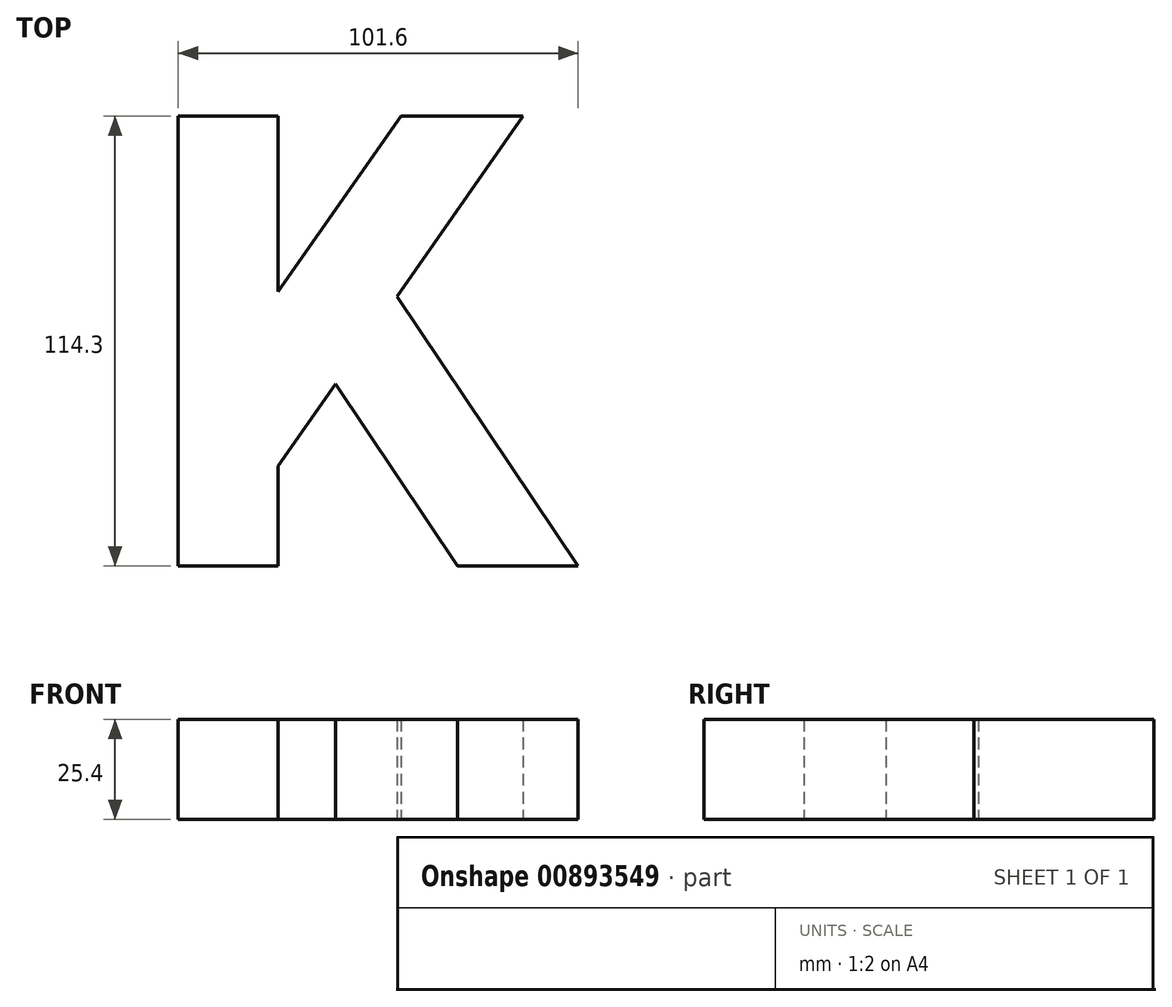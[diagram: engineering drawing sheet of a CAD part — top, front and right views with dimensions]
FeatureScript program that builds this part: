
annotation { "Feature Type Name" : "Feature", "Feature Type Description" : "" }
export const myFeature = defineFeature(function(context is Context, id is Id, definition is map)
    precondition{}
    {
        {
            var Q0;
            Q0=qCreatedBy(makeId("Top.planeOp"),FACE);
            var sketch = newSketch(context, id + "F0", { "sketchPlane" : qUnion([Q0])});
            skLineSegment(sketch, "E0", {"start": v(-39.97, 68.1) * mm, "end": v(-39.97, -46.2) * mm});
            skLineSegment(sketch, "E1", {"start": v(-39.97, -46.2) * mm, "end": v(-14.57, -46.2) * mm});
            skLineSegment(sketch, "E2", {"start": v(-14.57, -46.2) * mm, "end": v(-14.57, -20.8) * mm});
            skLineSegment(sketch, "E3", {"start": v(-14.57, -20.8) * mm, "end": v(0, 0) * mm});
            skLineSegment(sketch, "E4", {"start": v(0, 0) * mm, "end": v(31.03, -46.2) * mm});
            skLineSegment(sketch, "E5", {"start": v(31.03, -46.2) * mm, "end": v(61.63, -46.2) * mm});
            skLineSegment(sketch, "E6", {"start": v(61.63, -46.2) * mm, "end": v(15.62, 22.3) * mm});
            skLineSegment(sketch, "E7", {"start": v(15.62, 22.3) * mm, "end": v(47.68, 68.1) * mm});
            skLineSegment(sketch, "E8", {"start": v(47.68, 68.1) * mm, "end": v(16.67, 68.1) * mm});
            skLineSegment(sketch, "E9", {"start": v(16.67, 68.1) * mm, "end": v(-14.57, 23.48) * mm});
            skLineSegment(sketch, "E10", {"start": v(-14.57, 23.48) * mm, "end": v(-14.57, 68.1) * mm});
            skLineSegment(sketch, "E11", {"start": v(-14.57, 68.1) * mm, "end": v(-39.97, 68.1) * mm});
            skSolve(sketch);
        }
        {
            var Q0;
            Q0=makeQuery(id+"F0.imprint","IMPRINT",FACE,{"disambiguationData":[TD([[makeQuery(id+"F0.imprint","IMPRINT",EDGE,{"derivedFrom":sQuery(id+"F0.wireOp",EDGE,"E0")}),1.0]])]});
            extrude(context, id + "F1", {"entities" : qUnion([Q0]), "depth" : 25.4 * mm, "offsetDistance" : 25.4 * mm});
        }
    });
